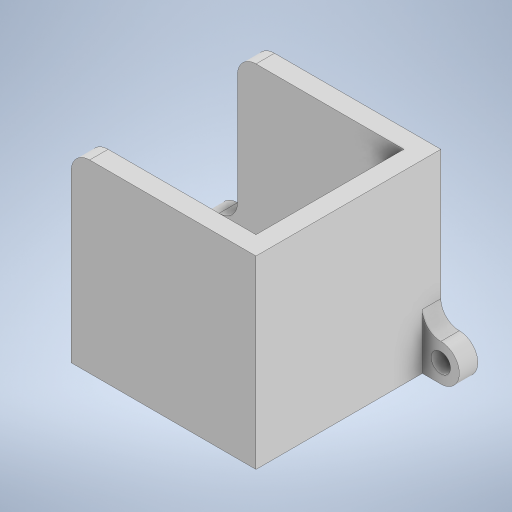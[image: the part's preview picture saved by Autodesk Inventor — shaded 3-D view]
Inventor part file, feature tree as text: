
AUTODESK INVENTOR PART (.ipt)
format: ipt  version: 2024 (Build 280153000, 153)  size: 233,984 bytes
history: native  units: mm
features: sketch x4, extrude x3, other x1, fillet x1, hole x1
ambient origin geometry x8: Origin, YZ Plane, XZ Plane, XY Plane, X Axis, Y Axis, Z Axis, Center Point
bodies: Body1 (feature_tree)
feature tree (10):
  other  "ソリッド1"
  extrude  "押し出し1"  Depth=50.0mm
  extrude  "押し出し2"  Depth=50.0mm
  extrude  "押し出し3"  Depth=50.0mm TaperAngle=0.0deg
  fillet  "フィレット1"  Radius=5.0mm
  hole  "穴1"  [1 undecoded]
  sketch  "スケッチ1"
  sketch  "スケッチ2"
  sketch  "スケッチ3"
  sketch  "スケッチ4"
note: 1 required parameter value undecoded (feature->parameter linkage not recoverable at this tier; creation-order binding heuristic only, values carry confidence <= 0.55)
